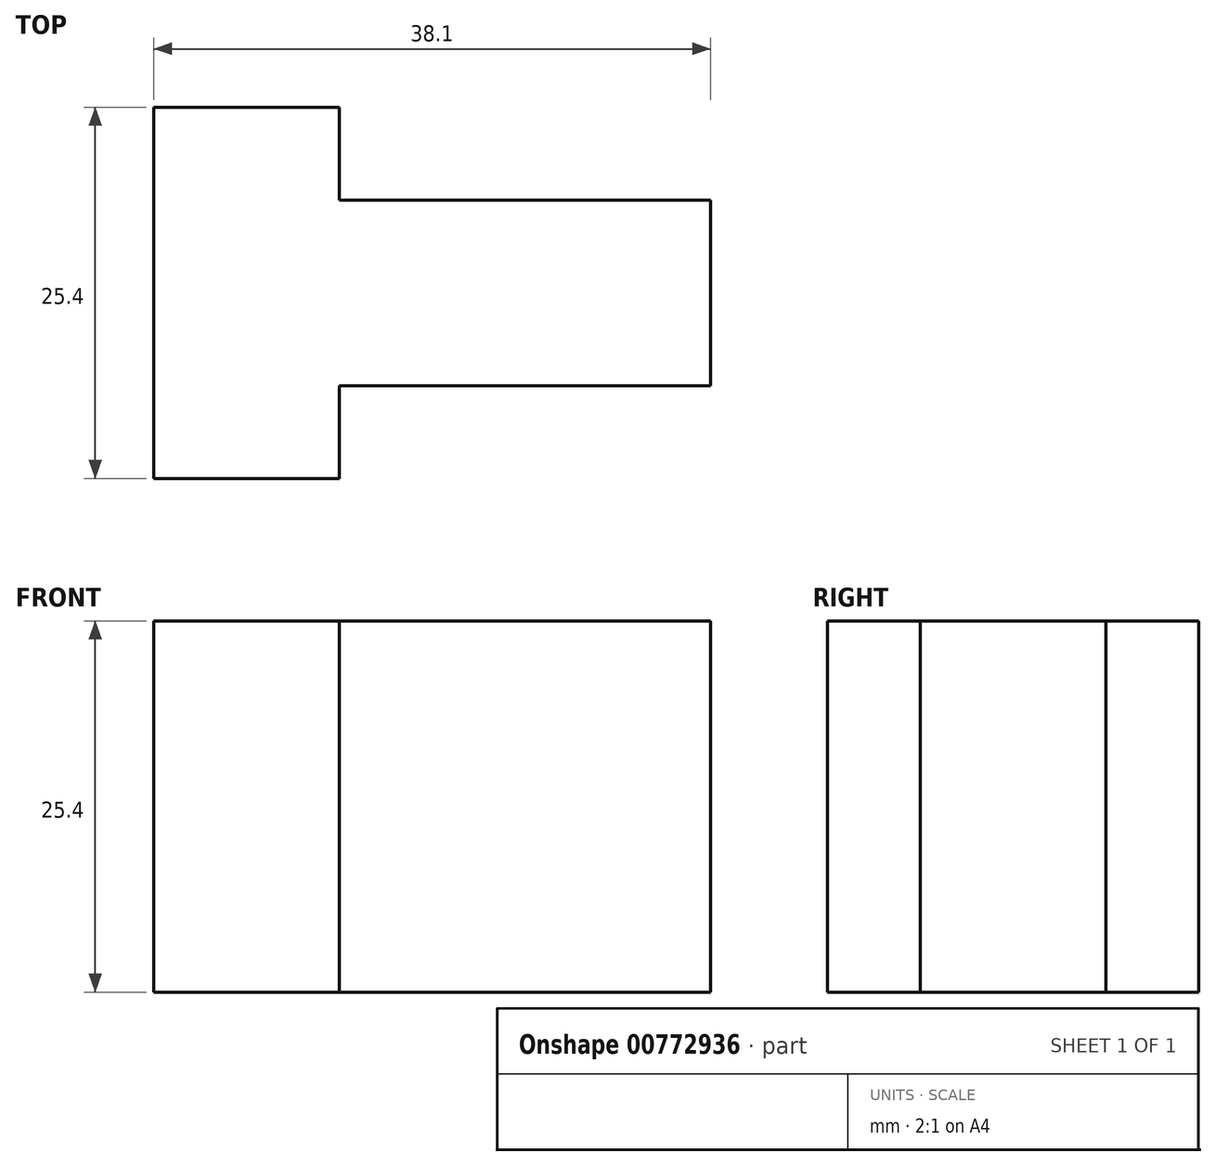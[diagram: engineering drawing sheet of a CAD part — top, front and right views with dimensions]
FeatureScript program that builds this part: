
annotation { "Feature Type Name" : "Feature", "Feature Type Description" : "" }
export const myFeature = defineFeature(function(context is Context, id is Id, definition is map)
    precondition{}
    {
        {
            var Q0;
            Q0=qCreatedBy(makeId("Top.planeOp"),FACE);
            var sketch = newSketch(context, id + "F0", { "sketchPlane" : qUnion([Q0])});
            skLineSegment(sketch, "E0", {"start": v(0, 0) * mm, "end": v(25.4, 0) * mm});
            skLineSegment(sketch, "E1", {"start": v(25.4, 12.7) * mm, "end": v(25.4, 0) * mm});
            skLineSegment(sketch, "E2", {"start": v(0, 12.7) * mm, "end": v(25.4, 12.7) * mm});
            skLineSegment(sketch, "E3", {"start": v(0, 19.05) * mm, "end": v(0, 12.7) * mm});
            skLineSegment(sketch, "E4", {"start": v(-12.7, 19.05) * mm, "end": v(0, 19.05) * mm});
            skLineSegment(sketch, "E5", {"start": v(0, -6.35) * mm, "end": v(0, 0) * mm});
            skLineSegment(sketch, "E6", {"start": v(-12.7, -6.35) * mm, "end": v(0, -6.35) * mm});
            skLineSegment(sketch, "E7", {"start": v(-12.7, -6.35) * mm, "end": v(-12.7, 19.05) * mm});
            skSolve(sketch);
        }
        {
            var Q0;
            Q0=makeQuery(id+"F0.imprint","IMPRINT",FACE,{"disambiguationData":[TD([[makeQuery(id+"F0.imprint","IMPRINT",EDGE,{"derivedFrom":sQuery(id+"F0.wireOp",EDGE,"E0")}),1.0]])]});
            extrude(context, id + "F1", {"entities" : qUnion([Q0]), "depth" : 25.4 * mm, "offsetDistance" : 25.4 * mm});
        }
    });
